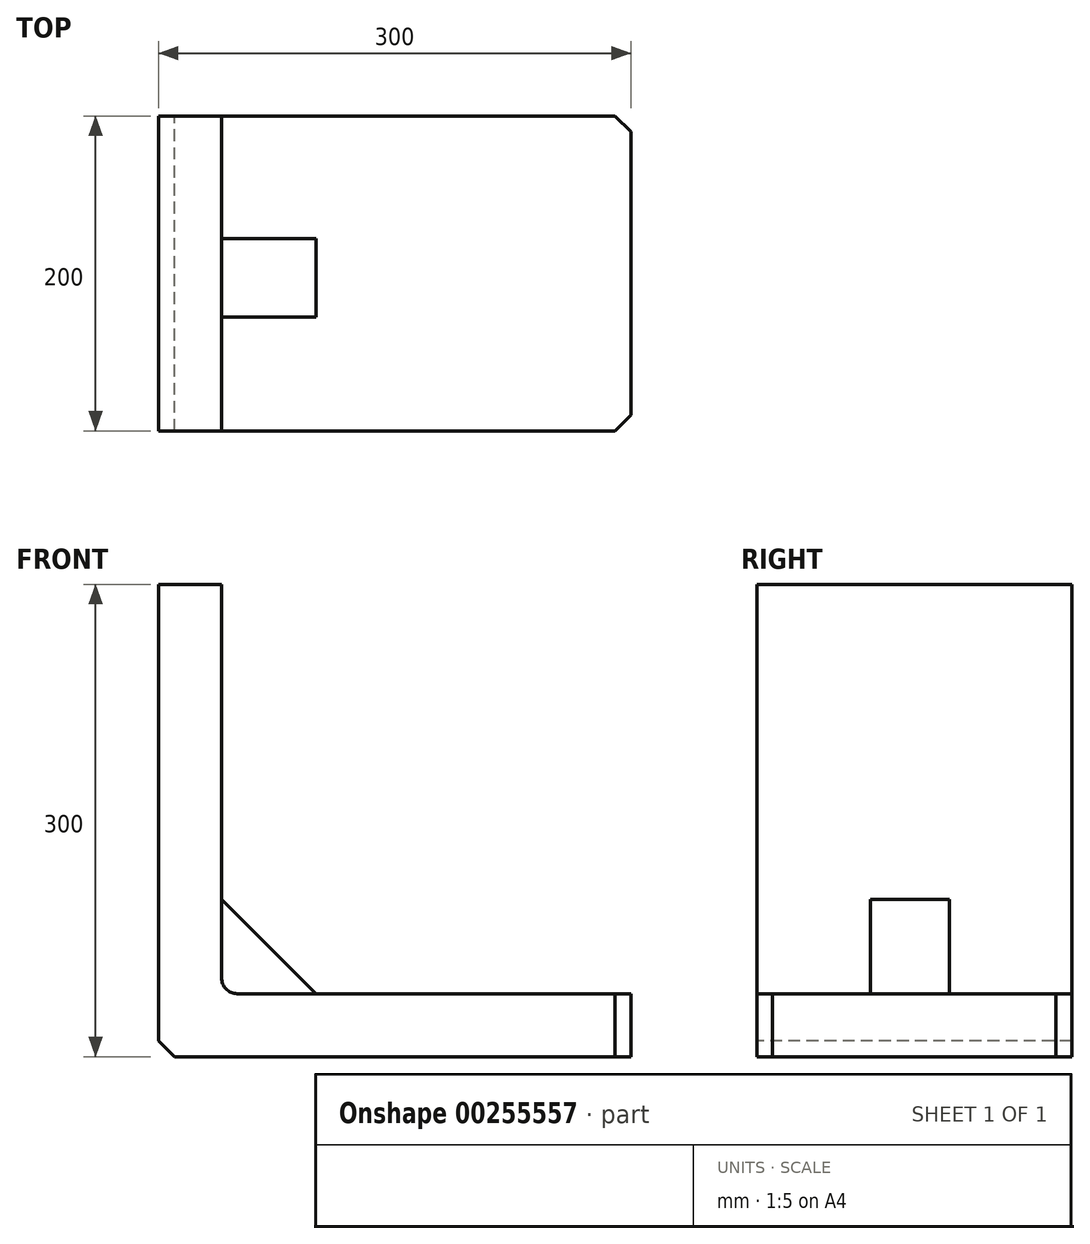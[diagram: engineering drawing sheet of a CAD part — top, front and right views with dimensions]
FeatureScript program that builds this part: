
annotation { "Feature Type Name" : "Feature", "Feature Type Description" : "" }
export const myFeature = defineFeature(function(context is Context, id is Id, definition is map)
    precondition{}
    {
        {
            var Q0;
            Q0=qCreatedBy(makeId("Top.planeOp"),FACE);
            var sketch = newSketch(context, id + "F0", { "sketchPlane" : qUnion([Q0])});
            skLineSegment(sketch, "E0.bottom", {"start": v(-151.44, 118.3) * mm, "end": v(148.56, 118.3) * mm});
            skLineSegment(sketch, "E0.top", {"start": v(-151.44, -81.7) * mm, "end": v(148.56, -81.7) * mm});
            skLineSegment(sketch, "E0.left", {"start": v(-151.44, 118.3) * mm, "end": v(-151.44, -81.7) * mm});
            skLineSegment(sketch, "E0.right", {"start": v(148.56, 118.3) * mm, "end": v(148.56, -81.7) * mm});
            skSolve(sketch);
        }
        {
            var Q0;
            Q0=makeQuery(id+"F0.imprint","IMPRINT",FACE,{"disambiguationData":[TD([[makeQuery(id+"F0.imprint","IMPRINT",EDGE,{"derivedFrom":sQuery(id+"F0.wireOp",EDGE,"E0.bottom")}),-1.0]])]});
            extrude(context, id + "F1", {"entities" : qUnion([Q0]), "depth" : 300 * mm});
        }
        {
            var Q0;
            Q0=makeQuery(id+"F1.opExtrude","CAP_FACE",FACE,{"disambiguationData":[OSD([sQuery(id+"F0.wireOp",EDGE,"E0.bottom"),sQuery(id+"F0.wireOp",EDGE,"E0.top"),sQuery(id+"F0.wireOp",EDGE,"E0.left"),sQuery(id+"F0.wireOp",EDGE,"E0.right")])],"isStart":false});
            var sketch = newSketch(context, id + "F2", { "sketchPlane" : qUnion([Q0])});
            skLineSegment(sketch, "E1.bottom", {"start": v(148.56, 118.3) * mm, "end": v(-111.44, 118.3) * mm});
            skLineSegment(sketch, "E1.top", {"start": v(148.56, -81.7) * mm, "end": v(-111.44, -81.7) * mm});
            skLineSegment(sketch, "E1.left", {"start": v(148.56, 118.3) * mm, "end": v(148.56, -81.7) * mm});
            skLineSegment(sketch, "E1.right", {"start": v(-111.44, 118.3) * mm, "end": v(-111.44, -81.7) * mm});
            skSolve(sketch);
        }
        {
            var Q0;
            Q0=makeQuery(id+"F2.imprint","IMPRINT",FACE,{"disambiguationData":[TD([[makeQuery(id+"F2.imprint","IMPRINT",EDGE,{"derivedFrom":sQuery(id+"F2.wireOp",EDGE,"E1.bottom")}),-1.0]])]});
            extrude(context, id + "F3", {"entities" : qUnion([Q0]), "operationType" : NewBodyOperationType.REMOVE, "oppositeDirection" : true, "depth" : 260 * mm});
        }
        {
            var Q0;
            Q0=makeQuery(id+"F3.boolean.opBoolean","COPY",EDGE,{"derivedFrom":makeQuery(id+"F3.opExtrude","CAP_EDGE",EDGE,{"disambiguationData":[OSD([sQuery(id+"F2.wireOp",EDGE,"E1.right")])],"isStart":false})});
            fillet(context, id + "F4", {"entities" : qUnion([Q0]), "radius" : 10 * mm, "tangentPropagation" : true, "allowEdgeOverflow" : false});
        }
        {
            var Q0;
            Q0=makeQuery(id+"F1.opExtrude","CAP_FACE",FACE,{"disambiguationData":[OSD([sQuery(id+"F0.wireOp",EDGE,"E0.bottom"),sQuery(id+"F0.wireOp",EDGE,"E0.top"),sQuery(id+"F0.wireOp",EDGE,"E0.left"),sQuery(id+"F0.wireOp",EDGE,"E0.right")])],"isStart":false});
            var sketch = newSketch(context, id + "F5", { "sketchPlane" : qUnion([Q0])});
            skLineSegment(sketch, "E2.bottom", {"start": v(-111.44, 40.55) * mm, "end": v(-51.44, 40.55) * mm});
            skLineSegment(sketch, "E2.top", {"start": v(-111.44, -9.45) * mm, "end": v(-51.44, -9.45) * mm});
            skLineSegment(sketch, "E2.left", {"start": v(-111.44, 40.55) * mm, "end": v(-111.44, -9.45) * mm});
            skLineSegment(sketch, "E2.right", {"start": v(-51.44, 40.55) * mm, "end": v(-51.44, -9.45) * mm});
            skSolve(sketch);
        }
        {
            var Q0;
            Q0=makeQuery(id+"F5.imprint","IMPRINT",FACE,{"disambiguationData":[TD([[makeQuery(id+"F5.imprint","IMPRINT",EDGE,{"derivedFrom":sQuery(id+"F5.wireOp",EDGE,"fxEpBx3H-iz6Q-G538-RA0t-bf7WLBaURCn5.bottom")}),-1.0]])]});
            var Q1;
            Q1=makeQuery(id+"F5.imprint","IMPRINT",FACE,{"disambiguationData":[TD([[makeQuery(id+"F5.imprint","IMPRINT",EDGE,{"derivedFrom":sQuery(id+"F5.wireOp",EDGE,"KQYSDmq7-Vo5K-FneR-G0ka-bRBcqd7utpTW.bottom")}),-1.0]])]});
            var Q2;
            Q2=makeQuery(id+"F5.imprint","IMPRINT",FACE,{"disambiguationData":[TD([[makeQuery(id+"F5.imprint","IMPRINT",EDGE,{"derivedFrom":sQuery(id+"F5.wireOp",EDGE,"E2.bottom")}),-1.0]])]});
            extrude(context, id + "F6", {"entities" : qUnion([Q0, Q1, Q2]), "operationType" : NewBodyOperationType.ADD, "oppositeDirection" : true, "depth" : 260 * mm});
        }
        {
            var Q0;
            Q0=makeQuery(id+"F1.opExtrude","CAP_EDGE",EDGE,{"disambiguationData":[OSD([sQuery(id+"F0.wireOp",EDGE,"E0.left")])],"isStart":true});
            var Q1;
            Q1=makeQuery(id+"F1.opExtrude","SWEPT_EDGE",EDGE,{"disambiguationData":[OSD([sQuery(id+"F0.wireOp",EDGE,"E0.top"),sQuery(id+"F0.wireOp",EDGE,"E0.right")])]});
            var Q2;
            Q2=makeQuery(id+"F1.opExtrude","SWEPT_EDGE",EDGE,{"disambiguationData":[OSD([sQuery(id+"F0.wireOp",EDGE,"E0.bottom"),sQuery(id+"F0.wireOp",EDGE,"E0.right")])]});
            chamfer(context, id + "F7", {"entities" : qUnion([Q0, Q1, Q2]), "width" : 10 * mm, "tangentPropagation" : true});
        }
        {
            var Q0;
            Q0=makeQuery(id+"F6.boolean.opBoolean","MERGE",FACE,{"derivedFrom":[makeQuery(id+"F1.opExtrude","CAP_FACE",FACE,{"disambiguationData":[OSD([sQuery(id+"F0.wireOp",EDGE,"E0.bottom"),sQuery(id+"F0.wireOp",EDGE,"E0.top"),sQuery(id+"F0.wireOp",EDGE,"E0.left"),sQuery(id+"F0.wireOp",EDGE,"E0.right")])],"isStart":false}),makeQuery(id+"F6.opExtrude","CAP_FACE",FACE,{"disambiguationData":[OSD([sQuery(id+"F5.wireOp",EDGE,"KQYSDmq7-Vo5K-FneR-G0ka-bRBcqd7utpTW.bottom"),sQuery(id+"F5.wireOp",EDGE,"KQYSDmq7-Vo5K-FneR-G0ka-bRBcqd7utpTW.top"),sQuery(id+"F5.wireOp",EDGE,"KQYSDmq7-Vo5K-FneR-G0ka-bRBcqd7utpTW.left"),sQuery(id+"F5.wireOp",EDGE,"KQYSDmq7-Vo5K-FneR-G0ka-bRBcqd7utpTW.right")])],"isStart":true})]});
            var sketch = newSketch(context, id + "F8", { "sketchPlane" : qUnion([Q0])});
            skLineSegment(sketch, "E3", {"start": v(-111.44, 40.55) * mm, "end": v(-111.44, 40.55) * mm});
            skLineSegment(sketch, "E4", {"start": v(-111.44, 40.55) * mm, "end": v(-111.44, -9.45) * mm});
            skSolve(sketch);
        }
        {
            var Q0;
            Q0=makeQuery(id+"F8.imprint","IMPRINT",FACE,{"disambiguationData":[TD([[makeQuery(id+"F8.imprint","IMPRINT",EDGE,{"derivedFrom":sQuery(id+"F8.wireOp",EDGE,"E3")}),1.0]])]});
            var Q1;
            Q1=makeQuery(id+"F8.imprint","IMPRINT",FACE,{"disambiguationData":[TD([[makeQuery(id+"F8.imprint","IMPRINT",EDGE,{"derivedFrom":sQuery(id+"F8.wireOp",EDGE,"E4")}),1.0]])]});
            extrude(context, id + "F9", {"entities" : qUnion([Q0, Q1]), "operationType" : NewBodyOperationType.REMOVE, "oppositeDirection" : true, "depth" : 200 * mm});
        }
        {
            var Q0;
            Q0=makeQuery(id+"F6.opExtrude","SWEPT_FACE",FACE,{"disambiguationData":[OSD([sQuery(id+"F5.wireOp",EDGE,"E2.top")])]});
            var sketch = newSketch(context, id + "F10", { "sketchPlane" : qUnion([Q0])});
            skLineSegment(sketch, "E5", {"start": v(-111.44, 100) * mm, "end": v(-51.44, 40) * mm});
            skSolve(sketch);
        }
        {
            var Q0;
            Q0=makeQuery(id+"F10.imprint","IMPRINT",FACE,{"disambiguationData":[TD([[makeQuery(id+"F10.imprint","IMPRINT",EDGE,{"derivedFrom":sQuery(id+"F10.wireOp",EDGE,"E5")}),1.0]])]});
            extrude(context, id + "F11", {"entities" : qUnion([Q0]), "operationType" : NewBodyOperationType.REMOVE, "oppositeDirection" : true, "depth" : 50 * mm});
        }
    });
